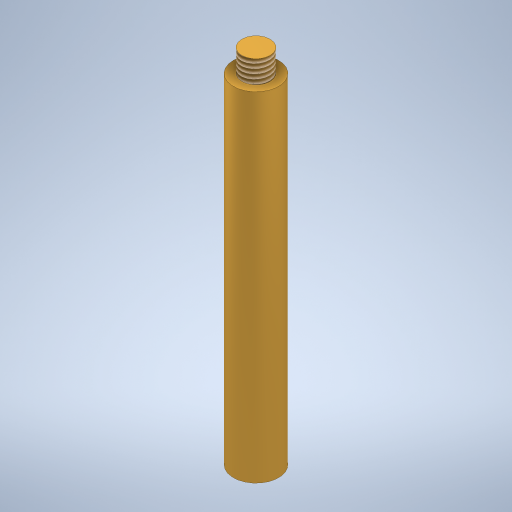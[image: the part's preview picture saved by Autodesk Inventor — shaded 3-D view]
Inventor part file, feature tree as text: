
AUTODESK INVENTOR PART (.ipt)
format: ipt  version: 2023.2 (Build 272271030, 271C)  size: 266,752 bytes
history: native  units: mm
features: extrude x3, thread x2, sketch x2, other x1
ambient origin geometry x8: Origin, YZ Plane, XZ Plane, XY Plane, X Axis, Y Axis, Z Axis, Center Point
bodies: Body1 (feature_tree)
feature tree (8):
  other  "Sólido1"
  extrude  "Extrusão1"  Depth=60.0mm TaperAngle=0.0deg
  extrude  "Extrusão2"  Depth=4.0mm TaperAngle=0.0deg
  thread  "Rosca1"  [1 undecoded]
  extrude  "Extrusão3"  Depth=15.0mm
  thread  "Rosca2"  [1 undecoded]
  sketch  "Esboço2"  dims[d1=8.0mm d2=60.0mm d3=0.0mm]
  sketch  "Esboço3"  dims[d4=5.0mm d5=4.0mm d6=0.0mm d7=5.0mm d8=0.0mm d9=5.0mm d10=15.0mm d11=0.0mm d12=15.0mm d13=0.0mm]
note: 2 required parameter values undecoded (feature->parameter linkage not recoverable at this tier; creation-order binding heuristic only, values carry confidence <= 0.55)
